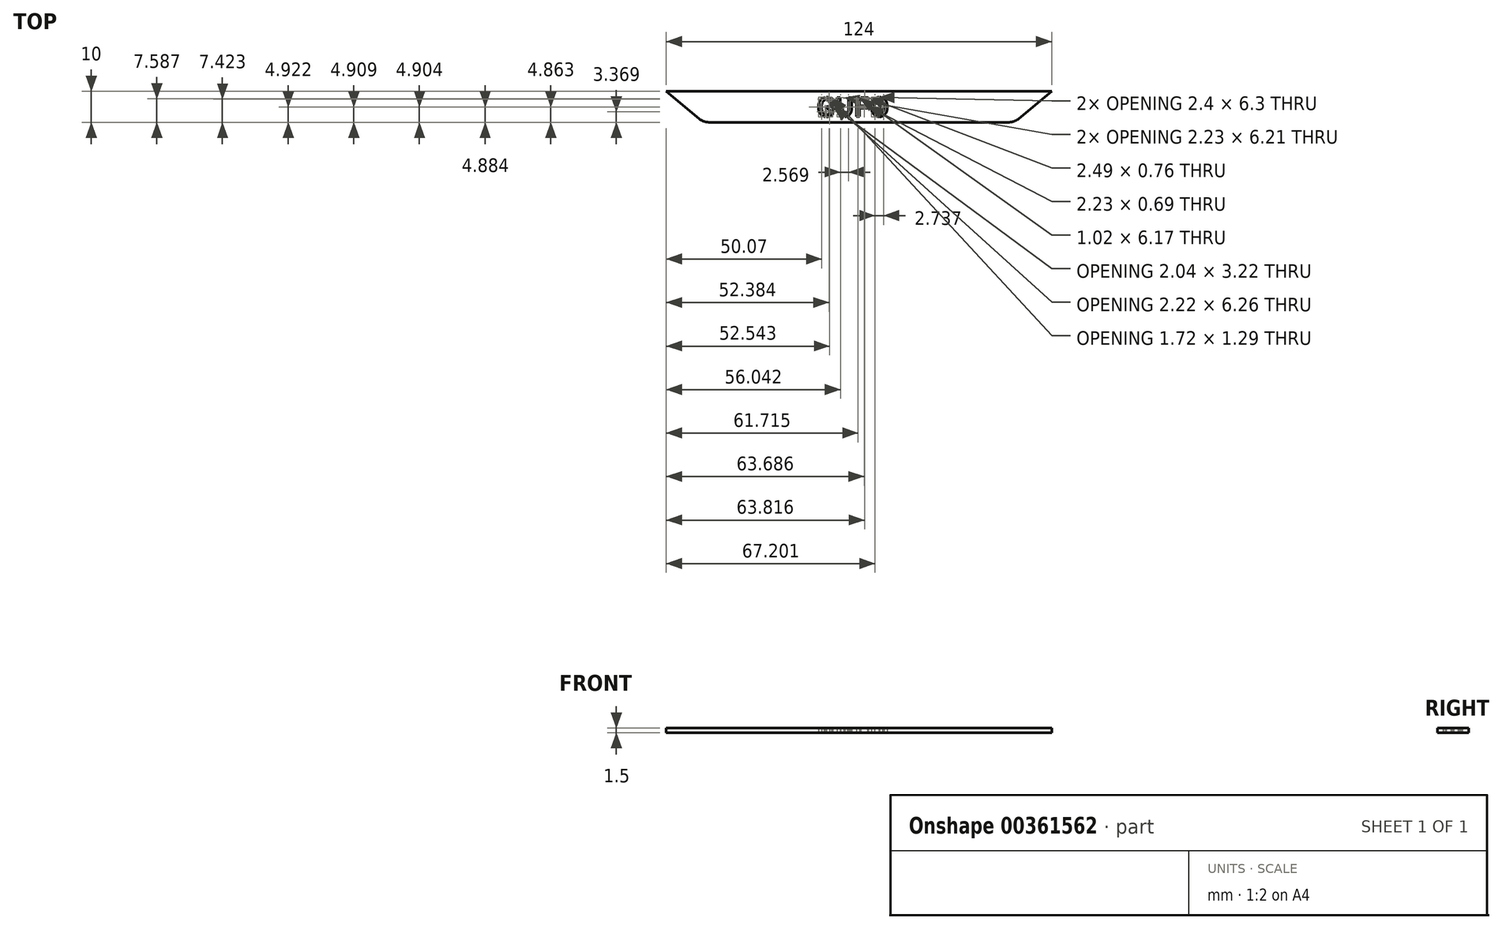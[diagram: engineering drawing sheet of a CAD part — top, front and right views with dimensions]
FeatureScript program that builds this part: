
annotation { "Feature Type Name" : "Feature", "Feature Type Description" : "" }
export const myFeature = defineFeature(function(context is Context, id is Id, definition is map)
    precondition{}
    {
        {
            var Q0;
            Q0=qCreatedBy(makeId("Top.planeOp"),FACE);
            var sketch = newSketch(context, id + "F0", { "sketchPlane" : qUnion([Q0])});
            skLineSegment(sketch, "E0.bottom", {"start": v(-48.19, -5) * mm, "end": v(48.19, -5) * mm});
            skLineSegment(sketch, "E0.top", {"start": v(-50, 5) * mm, "end": v(50, 5) * mm});
            skPoint(sketch, "E0.middle", {"position": v(0, 0) * mm});
            skLineSegment(sketch, "E1", {"start": v(-51.4, -3.84) * mm, "end": v(-62, 5) * mm});
            skLineSegment(sketch, "E2", {"start": v(-62, 5) * mm, "end": v(-50, 5) * mm});
            skLineSegment(sketch, "E3", {"start": v(51.4, -3.84) * mm, "end": v(62, 5) * mm});
            skLineSegment(sketch, "E4", {"start": v(62, 5) * mm, "end": v(50, 5) * mm});
            skPoint(sketch, "E5.visualSharp", {"position": v(-50, -5) * mm});
            skArc(sketch, "E5.filletArc", {"start": v(-51.4, -3.84) * mm, "mid": v(-49.9, -4.7) * mm, "end": v(-48.19, -5) * mm});
            skPoint(sketch, "E6.visualSharp", {"position": v(50, -5) * mm});
            skArc(sketch, "E6.filletArc", {"start": v(48.19, -5) * mm, "mid": v(49.9, -4.7) * mm, "end": v(51.4, -3.84) * mm});
            skText(sketch, "E7", { "text": "GUFO", "fontName": "AllertaStencil-Regular.ttf"});
            const initialGuessF0  = {"E7": [-0.0137, -0.0032, 1, 0, 0.00617]};
            skSetInitialGuess(sketch, initialGuessF0);
            skSolve(sketch);
        }
        {
            var Q0;
            Q0=makeQuery(id+"F0.imprint","IMPRINT",FACE,{"disambiguationData":[TD([[makeQuery(id+"F0.imprint","IMPRINT",EDGE,{"derivedFrom":sQuery(id+"F0.wireOp",EDGE,"E0.left")}),1.0]])]});
            var Q1;
            Q1=makeQuery(id+"F0.imprint","IMPRINT",FACE,{"disambiguationData":[TD([[makeQuery(id+"F0.imprint","IMPRINT",EDGE,{"derivedFrom":sQuery(id+"F0.wireOp",EDGE,"E0.bottom")}),1.0]])]});
            var Q2;
            Q2=makeQuery(id+"F0.imprint","IMPRINT",FACE,{"disambiguationData":[TD([[makeQuery(id+"F0.imprint","IMPRINT",EDGE,{"derivedFrom":sQuery(id+"F0.wireOp",EDGE,"E0.right")}),-1.0]])]});
            extrude(context, id + "F1", {"entities" : qUnion([Q0, Q1, Q2]), "depth" : 1.5 * mm});
        }
    });
